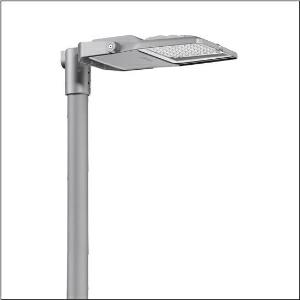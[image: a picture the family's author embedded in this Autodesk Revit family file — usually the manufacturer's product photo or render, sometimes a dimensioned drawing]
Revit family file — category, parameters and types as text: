
# Revit family: floodlight_fl_21_iq_mini___pl64_5xa7771c2e3a_b06c
name_source: partatom
category: Lighting Fixtures
units: mm (PartAtom-declared; Revit-internal decimal feet)

## family parameters
Cut with Voids When Loaded = No
Host = Face
Light Source = No
Part Type = Normal
Room Calculation Point = No
Round Connector Dimension = Use Diameter
Shared = No

## types (1)
- --- (1 x LED, 11790 lm, 87.2 W, 3000K)
    Apparent Load = 87 VA
    CIE Flux Codes = 28 80 98 100 100
    Color Rendering = 70
    Color Temperature = 3000K
    Default Elevation = 1800 mm
    Description = Floodlight FL 21 iQ mini, floodlight, primary light control with lens, of PMMA, primary optical cover: protective disc, of toughened safety glass, transparent, light distribution: PL64, light emission: direct distribution, installation type: surface-mounted, lamps: LED, High Power LED, rated values: 11.790lm | 87,2W | 135,2lm/W (begin service life); end service life: 11.790lm | 92,1W; at 50% lumin. flux: 5.895lm | 40,1W | 147lm/W, colour temperature: 3000K, colour rendering: CRI > 70, light colour: 730, light setting 1 begin service life: 100% | 11.790lm | 87,2W | 135,2lm/W | 3.000K, light setting 1 end service life: 92,1W, further light settings possible, control: Auto-Match, Temp-Guard, Lumen-Switch, Night-Set, Smart-Wire, Light-Fading, Desk-Remote (wireless, voltage-free reading and setting of iQ features in the workshop via application-optimized NFC function/RFID function), optimised constant luminous flux control (CLO 2.0), pre-setting: linear dimming characteristic, with terminal, 6-pole, mains connection: 220..240V, AC, 50/60Hz, luminaire housing, of diecast aluminium, powder-coated, SITECO metallic grey (DB 702S), corrosivity category C5 mid according to DIN EN ISO 12944suitable for swimming poolschlorine-resistant, sealing non-destructively replaceable, please order mast flange separately, mast bracket, of steel, galvanised, powder-coated, SITECO metallic grey (DB 702S), protection rating (complete): IP66, insulation class (complete): insulation class II (safety insulation), certification: CE, ENEC, VDE, protection symbol: D, impact resistance: IK08, permissible operating ambient temperature: -40..+40°C, permissible operating ambient temperature for outdoor applications: -40..+50°C, standard: DIN EN 12944, LABS conformity tested according to VDMA 24364:2018-05, packaging unit: 1 piece

Light Distribution: PL64
    Height = 70 mm
    Lamp = 1 x LED
    Lamp Light Flux = 11790 lm
    Lamp Power = 87.2 W
    Lamp count = 1
    Length = 485 mm
    Luminous efficacy = 135 lm/W
    Manufacturer = Siteco
    ModVariant = No
    Model = 5XA7771C2E3A
    Mounting Place = Pole
    Mounting Type = Pole annexe
    Number of Poles = 1
    OnlyDefault = Yes
    Power Factor = 1
    Product Name = Floodlight FL 21 iQ mini | PL64
    Product group = floodlight | pylon annexe
    ProductGroupID = 6201
    Protection Class = Protection class II
    Protection Degree = IP 66
    RLX_Detail_Level = 1
    RLX_Emergency_Light_Flux = 0 lm
    RLX_Emergency_Type = 0
    RLX_Emergency_Type_DB = No
    RlxData = <blob elided: 101637 chars, md5=73047093>
    Socket = socket
    Standby Power = 0 W
    System Light Flux = 11790 lm
    System Power = 87 W
    Type Comments = factory setting: luminous flux: 100 % | dim-lin: 254 | 456 mA
    Type Image = l_1007125.jpg
    URL = http://relux.com
    VarID = @adj_167647
    Voltage = 0 V
    Weight = 0.00 kg
    Width = 337 mm

## geometry (parser evidence)
native form markers: Blend x4, Sweep x13
no freeform markers — native parametric forms only
